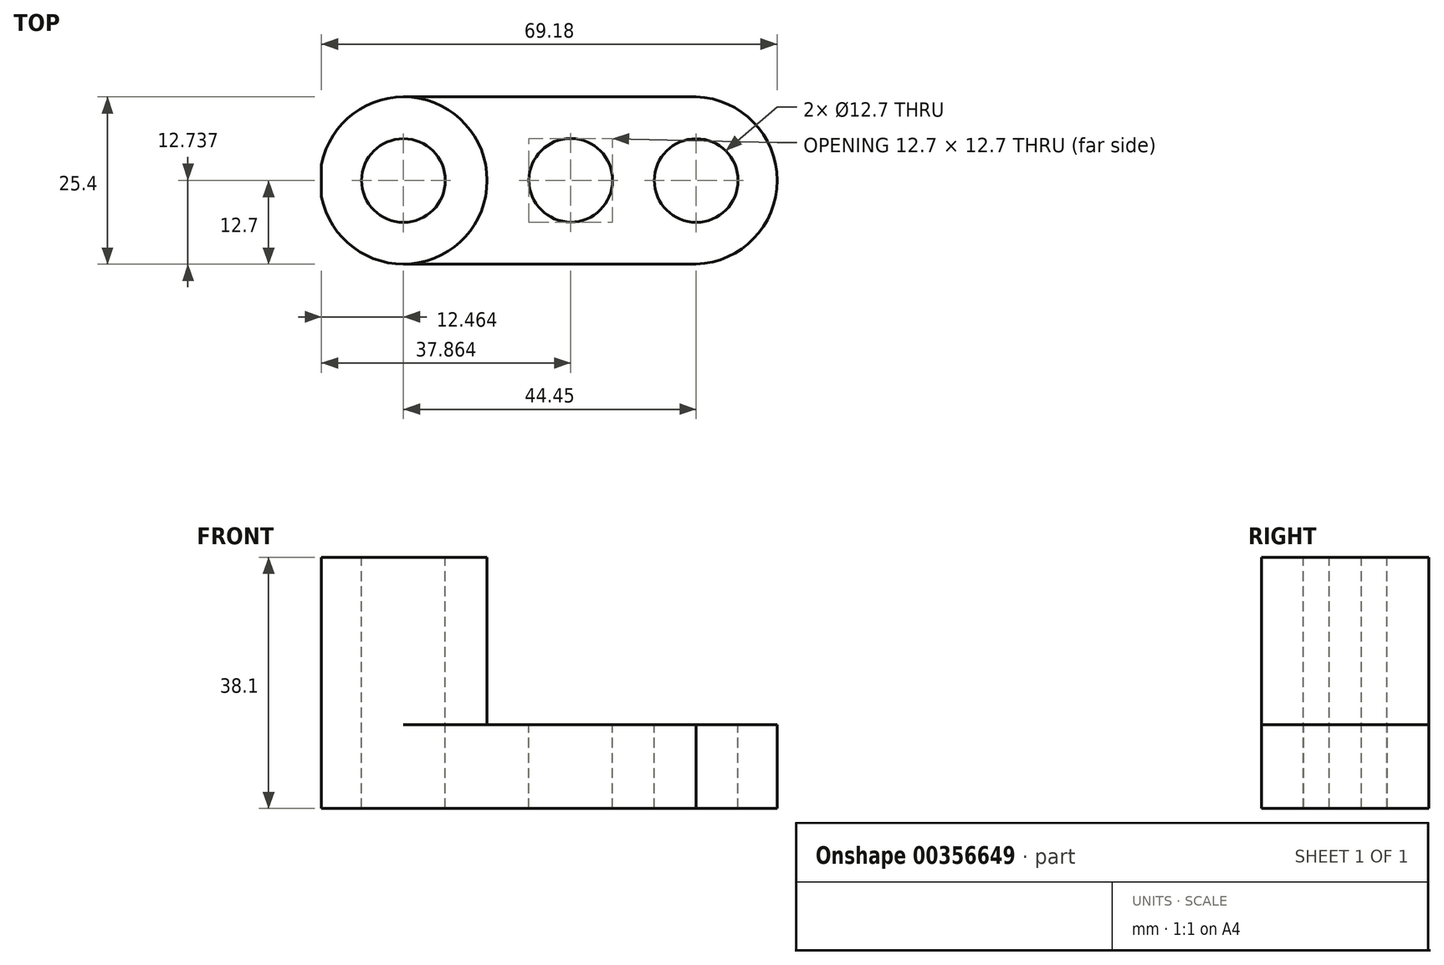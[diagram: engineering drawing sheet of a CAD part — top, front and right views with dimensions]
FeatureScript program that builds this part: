
annotation { "Feature Type Name" : "Feature", "Feature Type Description" : "" }
export const myFeature = defineFeature(function(context is Context, id is Id, definition is map)
    precondition{}
    {
        {
            var Q0;
            Q0=qCreatedBy(makeId("Front.planeOp"),FACE);
            var sketch = newSketch(context, id + "F0", { "sketchPlane" : qUnion([Q0])});
            skLineSegment(sketch, "E0", {"start": v(0, 0) * mm, "end": v(69.85, 0) * mm});
            skLineSegment(sketch, "E1", {"start": v(69.85, 0) * mm, "end": v(69.85, 12.7) * mm});
            skLineSegment(sketch, "E2", {"start": v(69.85, 12.7) * mm, "end": v(25.4, 12.7) * mm});
            skLineSegment(sketch, "E3", {"start": v(25.4, 12.7) * mm, "end": v(25.4, 38.1) * mm});
            skLineSegment(sketch, "E4", {"start": v(25.4, 38.1) * mm, "end": v(0, 38.1) * mm});
            skLineSegment(sketch, "E5", {"start": v(0, 38.1) * mm, "end": v(0, 0) * mm});
            skSolve(sketch);
        }
        {
            var Q0;
            Q0=makeQuery(id+"F0.imprint","IMPRINT",FACE,{"disambiguationData":[TD([[makeQuery(id+"F0.imprint","IMPRINT",EDGE,{"derivedFrom":sQuery(id+"F0.wireOp",EDGE,"E0")}),1.0]])]});
            extrude(context, id + "F1", {"entities" : qUnion([Q0]), "depth" : 25.4 * mm});
        }
        {
            var Q0;
            Q0=makeQuery(id+"F1.opExtrude","SWEPT_FACE",FACE,{"disambiguationData":[OSD([sQuery(id+"F0.wireOp",EDGE,"E4")])]});
            var sketch = newSketch(context, id + "F2", { "sketchPlane" : qUnion([Q0])});
            skCircle(sketch, "E6", {"center": v(12.46, -12.7) * mm, "radius": 12.7 * mm});
            skPoint(sketch, "E6.centerSnap0", {"position": v(0, -12.7) * mm});
            skCircle(sketch, "E7", {"center": v(12.46, -12.7) * mm, "radius": 6.35 * mm});
            skSolve(sketch);
        }
        {
            var Q0;
            {var subQ1=sQuery(id+"F0.wireOp",EDGE,"E4");var subQ6=makeQuery(id+"F1.opExtrude","SWEPT_EDGE",EDGE,{"disambiguationData":[OSD([sQuery(id+"F0.wireOp",EDGE,"E3"),subQ1])]});Q0=makeQuery(id+"F2.imprint","IMPRINT",FACE,{"disambiguationData":[TD([[makeQuery(id+"F2.imprint","IMPRINT",EDGE,{"derivedFrom":subQ6}),1.0]])]});}
            var Q1;
            {var subQ0=sQuery(id+"F2.wireOp",EDGE,"E6");var subQ1=sQuery(id+"F0.wireOp",EDGE,"E4");var subQ4=makeQuery(id+"F1.opExtrude","CAP_EDGE",EDGE,{"disambiguationData":[OSD([subQ1])],"isStart":true});var subQ5=makeQuery(id+"F2.imprint","INTERSECT",VERTEX,{"derivedFrom":[subQ4,subQ0]});Q1=makeQuery(id+"F2.imprint","IMPRINT",FACE,{"disambiguationData":[TD([[makeQuery(id+"F2.imprint","IMPRINT",EDGE,{"disambiguationData":[TD([[subQ5,-1.0]])],"derivedFrom":subQ0}),-1.0]])]});}
            var Q2;
            {var subQ0=sQuery(id+"F2.wireOp",EDGE,"E6");var subQ1=sQuery(id+"F0.wireOp",EDGE,"E4");var subQ4=makeQuery(id+"F1.opExtrude","CAP_EDGE",EDGE,{"disambiguationData":[OSD([subQ1])],"isStart":false});var subQ5=makeQuery(id+"F2.imprint","INTERSECT",VERTEX,{"derivedFrom":[subQ4,subQ0]});Q2=makeQuery(id+"F2.imprint","IMPRINT",FACE,{"disambiguationData":[TD([[makeQuery(id+"F2.imprint","IMPRINT",EDGE,{"disambiguationData":[TD([[subQ5,1.0]])],"derivedFrom":subQ0}),-1.0]])]});}
            extrude(context, id + "F3", {"entities" : qUnion([Q0, Q1, Q2]), "operationType" : NewBodyOperationType.REMOVE, "oppositeDirection" : true, "depth" : 25.4 * mm});
        }
        {
            var Q0;
            Q0=makeQuery(id+"F1.opExtrude","SWEPT_FACE",FACE,{"disambiguationData":[OSD([sQuery(id+"F0.wireOp",EDGE,"E4")])]});
            var sketch = newSketch(context, id + "F4", { "sketchPlane" : qUnion([Q0])});
            skCircle(sketch, "E8", {"center": v(12.46, -12.7) * mm, "radius": 6.35 * mm});
            skSolve(sketch);
        }
        {
            var Q0;
            Q0=makeQuery(id+"F4.imprint","IMPRINT",FACE,{"disambiguationData":[TD([[makeQuery(id+"F4.imprint","IMPRINT",EDGE,{"derivedFrom":sQuery(id+"F4.wireOp",EDGE,"E8")}),1.0]])]});
            extrude(context, id + "F5", {"entities" : qUnion([Q0]), "operationType" : NewBodyOperationType.REMOVE, "oppositeDirection" : true, "depth" : 50.8 * mm});
        }
        {
            var Q0;
            {var subQ0=sQuery(id+"F0.wireOp",EDGE,"E4");var subQ1=makeQuery(id+"F1.opExtrude","CAP_EDGE",EDGE,{"disambiguationData":[OSD([subQ0])],"isStart":true});var subQ2=sQuery(id+"F0.wireOp",EDGE,"E5");var subQ3=makeQuery(id+"F1.opExtrude","SWEPT_EDGE",EDGE,{"disambiguationData":[OSD([subQ0,subQ2])]});var subQ4=makeQuery(id+"F2.imprint","INTERSECT",VERTEX,{"derivedFrom":[subQ3,subQ1]});var subQ5=sQuery(id+"F2.wireOp",EDGE,"E6");var subQ6=makeQuery(id+"F2.imprint","INTERSECT",VERTEX,{"derivedFrom":[subQ1,subQ5]});Q0=makeQuery(id+"F3.boolean.opBoolean","COPY",FACE,{"derivedFrom":makeQuery(id+"F3.opExtrude","CAP_FACE",FACE,{"disambiguationData":[OSD([subQ0,subQ2,subQ5]),TDD([makeQuery(id+"F2.imprint","IMPRINT",EDGE,{"disambiguationData":[TD([[subQ6,-1.0]])],"derivedFrom":subQ5}),makeQuery(id+"F2.imprint","IMPRINT",EDGE,{"disambiguationData":[TD([[subQ4,1.0]])],"derivedFrom":subQ3}),makeQuery(id+"F2.imprint","IMPRINT",EDGE,{"disambiguationData":[TD([[subQ6,-1.0]])],"derivedFrom":subQ1})])],"isStart":false})});}
            var sketch = newSketch(context, id + "F6", { "sketchPlane" : qUnion([Q0])});
            skArc(sketch, "E9", {"start": v(12.46, 0) * mm, "mid": v(-0.2, -12.66) * mm, "end": v(12.46, -25.33) * mm});
            skSolve(sketch);
        }
        {
            var Q0;
            {var subQ0=sQuery(id+"F2.wireOp",EDGE,"E6");var subQ2=sQuery(id+"F0.wireOp",EDGE,"E4");var subQ5=makeQuery(id+"F1.opExtrude","CAP_EDGE",EDGE,{"disambiguationData":[OSD([subQ2])],"isStart":true});var subQ6=makeQuery(id+"F2.imprint","INTERSECT",VERTEX,{"derivedFrom":[subQ5,subQ0]});Q0=makeQuery(id+"F6.imprint","IMPRINT",FACE,{"disambiguationData":[TD([[makeQuery(id+"F6.imprint","IMPRINT",EDGE,{"derivedFrom":makeQuery(id+"F3.boolean.opBoolean","COPY",EDGE,{"derivedFrom":makeQuery(id+"F3.opExtrude","CAP_EDGE",EDGE,{"disambiguationData":[OSD([subQ0]),TDD([makeQuery(id+"F2.imprint","IMPRINT",EDGE,{"disambiguationData":[TD([[subQ6,-1.0]])],"derivedFrom":subQ0})])],"isStart":false})})}),-1.0]])]});}
            var Q1;
            {var subQ0=sQuery(id+"F0.wireOp",EDGE,"E4");var subQ1=makeQuery(id+"F1.opExtrude","CAP_EDGE",EDGE,{"disambiguationData":[OSD([subQ0])],"isStart":false});var subQ2=sQuery(id+"F0.wireOp",EDGE,"E5");var subQ3=makeQuery(id+"F1.opExtrude","SWEPT_EDGE",EDGE,{"disambiguationData":[OSD([subQ0,subQ2])]});var subQ4=makeQuery(id+"F2.imprint","INTERSECT",VERTEX,{"derivedFrom":[subQ3,subQ1]});var subQ5=sQuery(id+"F2.wireOp",EDGE,"E6");var subQ6=makeQuery(id+"F2.imprint","INTERSECT",VERTEX,{"derivedFrom":[subQ1,subQ5]});Q1=makeQuery(id+"F3.boolean.opBoolean","COPY",FACE,{"derivedFrom":makeQuery(id+"F3.opExtrude","CAP_FACE",FACE,{"disambiguationData":[OSD([subQ0,subQ2,subQ5]),TDD([makeQuery(id+"F2.imprint","IMPRINT",EDGE,{"disambiguationData":[TD([[subQ6,1.0]])],"derivedFrom":subQ5}),makeQuery(id+"F2.imprint","IMPRINT",EDGE,{"disambiguationData":[TD([[subQ4,-1.0]])],"derivedFrom":subQ3}),makeQuery(id+"F2.imprint","IMPRINT",EDGE,{"disambiguationData":[TD([[subQ6,-1.0]])],"derivedFrom":subQ1})])],"isStart":false})});}
            extrude(context, id + "F7", {"entities" : qUnion([Q0, Q1]), "operationType" : NewBodyOperationType.REMOVE, "oppositeDirection" : true, "depth" : 1752.6 * mm});
        }
        {
            var Q0;
            Q0=makeQuery(id+"F3.boolean.opBoolean","MERGE",FACE,{"derivedFrom":[makeQuery(id+"F1.opExtrude","SWEPT_FACE",FACE,{"disambiguationData":[OSD([sQuery(id+"F0.wireOp",EDGE,"E2")])]}),makeQuery(id+"F3.opExtrude","CAP_FACE",FACE,{"disambiguationData":[OSD([sQuery(id+"F0.wireOp",EDGE,"E3"),sQuery(id+"F0.wireOp",EDGE,"E4"),sQuery(id+"F2.wireOp",EDGE,"E6")])],"isStart":false})]});
            var sketch = newSketch(context, id + "F8", { "sketchPlane" : qUnion([Q0])});
            skCircle(sketch, "E10", {"center": v(37.86, -12.66) * mm, "radius": 6.35 * mm});
            skCircle(sketch, "E11", {"center": v(56.91, -12.7) * mm, "radius": 6.35 * mm});
            skArc(sketch, "E12", {"start": v(56.91, -25.4) * mm, "mid": v(69.18, -12.7) * mm, "end": v(56.91, 0) * mm});
            skLineSegment(sketch, "E13", {"start": v(37.86, -6.31) * mm, "end": v(56.93, -6.35) * mm});
            skLineSegment(sketch, "E14", {"start": v(37.86, -19.01) * mm, "end": v(56.91, -19.01) * mm});
            skSolve(sketch);
        }
        {
            var Q0;
            {var subQ0=sQuery(id+"F8.wireOp",EDGE,"E10");var subQ2=makeQuery(id+"F8.imprint","IMPRINT",VERTEX,{"derivedFrom":subQ0});Q0=makeQuery(id+"F8.imprint","IMPRINT",FACE,{"disambiguationData":[TD([[makeQuery(id+"F8.imprint","IMPRINT",EDGE,{"disambiguationData":[TD([[subQ2,1.0]])],"derivedFrom":subQ0}),1.0]])]});}
            var Q1;
            {var subQ0=sQuery(id+"F8.wireOp",EDGE,"E13");Q1=makeQuery(id+"F8.imprint","IMPRINT",FACE,{"disambiguationData":[TD([[makeQuery(id+"F8.imprint","IMPRINT",EDGE,{"derivedFrom":subQ0}),-1.0]])]});}
            var Q2;
            {var subQ0=sQuery(id+"F8.wireOp",EDGE,"E11");var subQ1=makeQuery(id+"F8.imprint","INTERSECT",VERTEX,{"derivedFrom":[subQ0,sQuery(id+"F8.wireOp",EDGE,"E13")]});Q2=makeQuery(id+"F8.imprint","IMPRINT",FACE,{"disambiguationData":[TD([[makeQuery(id+"F8.imprint","IMPRINT",EDGE,{"disambiguationData":[TD([[subQ1,-1.0]])],"derivedFrom":subQ0}),1.0]])]});}
            var Q3;
            {var subQ0=sQuery(id+"F8.wireOp",EDGE,"E12");Q3=makeQuery(id+"F8.imprint","IMPRINT",FACE,{"disambiguationData":[TD([[makeQuery(id+"F8.imprint","IMPRINT",EDGE,{"derivedFrom":subQ0}),-1.0]])]});}
            extrude(context, id + "F9", {"entities" : qUnion([Q0, Q1, Q2, Q3]), "operationType" : NewBodyOperationType.REMOVE, "oppositeDirection" : true, "depth" : 1752.6 * mm});
        }
    });
